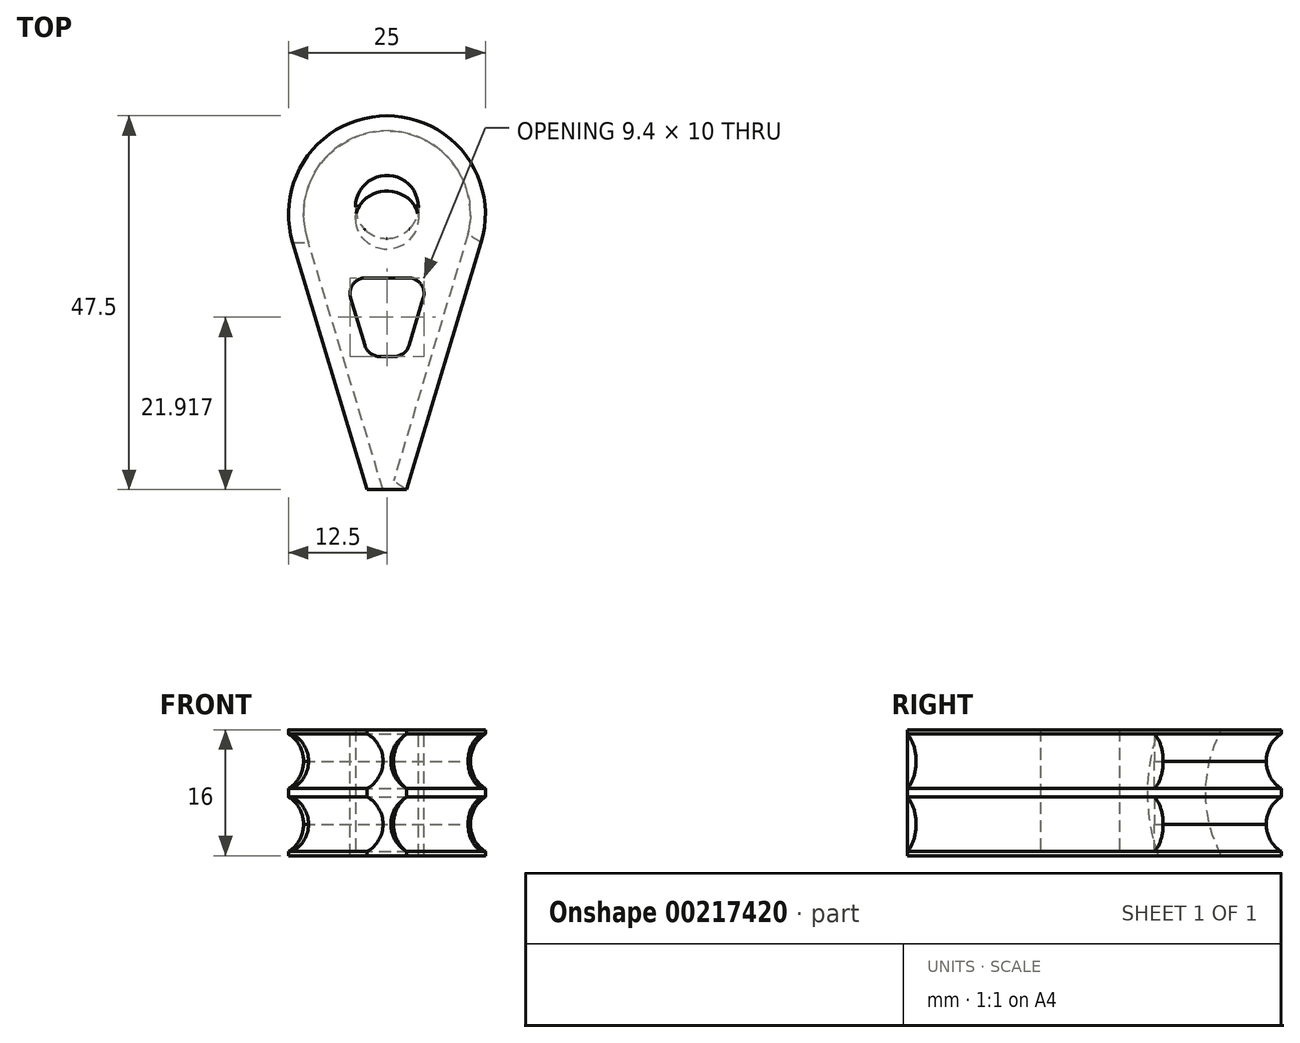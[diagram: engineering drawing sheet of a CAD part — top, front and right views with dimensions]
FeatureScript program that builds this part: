
annotation { "Feature Type Name" : "Feature", "Feature Type Description" : "" }
export const myFeature = defineFeature(function(context is Context, id is Id, definition is map)
    precondition{}
    {
        {
            var Q0;
            Q0=qCreatedBy(makeId("Top.planeOp"),FACE);
            var sketch = newSketch(context, id + "F0", { "sketchPlane" : qUnion([Q0])});
            skArc(sketch, "E0", {"start": v(11.97, -3.6) * mm, "mid": v(0, 12.5) * mm, "end": v(-11.97, -3.6) * mm});
            skLineSegment(sketch, "E1", {"start": v(-11.97, -3.6) * mm, "end": v(-2.5, -35) * mm});
            skLineSegment(sketch, "E2", {"start": v(-2.5, -35) * mm, "end": v(2.5, -35) * mm});
            skLineSegment(sketch, "E3", {"start": v(2.5, -35) * mm, "end": v(11.97, -3.6) * mm});
            skSolve(sketch);
        }
        {
            var Q0;
            Q0=makeQuery(id+"F0.imprint","IMPRINT",FACE,{"disambiguationData":[TD([[makeQuery(id+"F0.imprint","IMPRINT",EDGE,{"derivedFrom":sQuery(id+"F0.wireOp",EDGE,"E0")}),1.0]])]});
            extrude(context, id + "F1", {"entities" : qUnion([Q0]), "depth" : 4 * mm});
        }
        {
            var Q0;
            Q0=makeQuery(id+"F1.opExtrude","CAP_FACE",FACE,{"disambiguationData":[OSD([sQuery(id+"F0.wireOp",EDGE,"C9fcvXtV-jNcn-DBfI-eW0K-3YuiEhr3QxEZ"),sQuery(id+"F0.wireOp",EDGE,"E0"),sQuery(id+"F0.wireOp",EDGE,"E1"),sQuery(id+"F0.wireOp",EDGE,"E2"),sQuery(id+"F0.wireOp",EDGE,"E3")])],"isStart":false});
            var sketch = newSketch(context, id + "F2", { "sketchPlane" : qUnion([Q0])});
            skLineSegment(sketch, "E4", {"start": v(2.5, -35) * mm, "end": v(0.34, -42.16) * mm});
            skSolve(sketch);
        }
        {
            var Q0;
            Q0=makeQuery(id+"F1.opExtrude","SWEPT_FACE",FACE,{"disambiguationData":[OSD([sQuery(id+"F0.wireOp",EDGE,"E2")])]});
            var sketch = newSketch(context, id + "F3", { "sketchPlane" : qUnion([Q0])});
            skCircle(sketch, "E5", {"center": v(-4.5, 4) * mm, "radius": 4 * mm});
            skSolve(sketch);
        }
        {
            var Q0;
            {var subQ0=sQuery(id+"F3.wireOp",EDGE,"E5");var subQ1=sQuery(id+"F0.wireOp",EDGE,"E2");var subQ4=makeQuery(id+"F1.opExtrude","CAP_EDGE",EDGE,{"disambiguationData":[OSD([subQ1])],"isStart":false});var subQ5=makeQuery(id+"F3.imprint","INTERSECT",VERTEX,{"derivedFrom":[subQ4,subQ0]});Q0=makeQuery(id+"F3.imprint","IMPRINT",FACE,{"disambiguationData":[TD([[makeQuery(id+"F3.imprint","IMPRINT",EDGE,{"disambiguationData":[TD([[subQ5,1.0]])],"derivedFrom":subQ0}),1.0]])]});}
            var Q1;
            Q1=sQuery(id+"F3.wireOp",EDGE,"E5");
            var Q2;
            Q2=makeQuery(id+"F1.opExtrude","CAP_EDGE",EDGE,{"disambiguationData":[OSD([sQuery(id+"F0.wireOp",EDGE,"E1")])],"isStart":false});
            var Q3;
            Q3=makeQuery(id+"F1.opExtrude","CAP_EDGE",EDGE,{"disambiguationData":[OSD([sQuery(id+"F0.wireOp",EDGE,"E0")])],"isStart":false});
            var Q4;
            Q4=makeQuery(id+"F1.opExtrude","CAP_EDGE",EDGE,{"disambiguationData":[OSD([sQuery(id+"F0.wireOp",EDGE,"E3")])],"isStart":false});
            var Q5;
            Q5=sQuery(id+"F2.wireOp",EDGE,"E4");
            sweep(context, id + "F4", {"operationType" : NewBodyOperationType.REMOVE, "profiles" : qUnion([Q0]), "surfaceProfiles" : qUnion([Q1]), "path" : qUnion([Q2, Q3, Q4, Q5])});
        }
        {
            var Q0;
            Q0=makeQuery(id+"F1.opExtrude","SWEPT_BODY",BODY,{"disambiguationData":[OSD([sQuery(id+"F0.wireOp",EDGE,"C9fcvXtV-jNcn-DBfI-eW0K-3YuiEhr3QxEZ"),sQuery(id+"F0.wireOp",EDGE,"E0"),sQuery(id+"F0.wireOp",EDGE,"E1"),sQuery(id+"F0.wireOp",EDGE,"E2"),sQuery(id+"F0.wireOp",EDGE,"E3")])]});
            var Q1;
            Q1=makeQuery(id+"F1.opExtrude","CAP_FACE",FACE,{"disambiguationData":[OSD([sQuery(id+"F0.wireOp",EDGE,"C9fcvXtV-jNcn-DBfI-eW0K-3YuiEhr3QxEZ"),sQuery(id+"F0.wireOp",EDGE,"E0"),sQuery(id+"F0.wireOp",EDGE,"E1"),sQuery(id+"F0.wireOp",EDGE,"E2"),sQuery(id+"F0.wireOp",EDGE,"E3")])],"isStart":false});
            mirror(context, id + "F5", {"operationType" : NewBodyOperationType.ADD, "entities" : qUnion([Q0]), "mirrorPlane" : qUnion([Q1])});
        }
        {
            var Q0;
            Q0=makeQuery(id+"F1.opExtrude","SWEPT_BODY",BODY,{"disambiguationData":[OSD([sQuery(id+"F0.wireOp",EDGE,"E0"),sQuery(id+"F0.wireOp",EDGE,"E1"),sQuery(id+"F0.wireOp",EDGE,"E2"),sQuery(id+"F0.wireOp",EDGE,"E3")])]});
            var Q1;
            Q1=makeQuery(id+"F1.opExtrude","CAP_FACE",FACE,{"disambiguationData":[OSD([sQuery(id+"F0.wireOp",EDGE,"E0"),sQuery(id+"F0.wireOp",EDGE,"E1"),sQuery(id+"F0.wireOp",EDGE,"E2"),sQuery(id+"F0.wireOp",EDGE,"E3")])],"isStart":true});
            mirror(context, id + "F6", {"operationType" : NewBodyOperationType.ADD, "entities" : qUnion([Q0]), "mirrorPlane" : qUnion([Q1])});
        }
        {
            var Q0;
            Q0=qCreatedBy(makeId("Right.planeOp"),FACE);
            var sketch = newSketch(context, id + "F7", { "sketchPlane" : qUnion([Q0])});
            skCircle(sketch, "E6", {"center": v(20, 0) * mm, "radius": 20 * mm});
            skSolve(sketch);
        }
        {
            var Q0;
            Q0=makeQuery(id+"F6.opPattern","COPY",FACE,{"derivedFrom":makeQuery(id+"F5.opPattern","COPY",FACE,{"derivedFrom":makeQuery(id+"F1.opExtrude","CAP_FACE",FACE,{"disambiguationData":[OSD([sQuery(id+"F0.wireOp",EDGE,"E0"),sQuery(id+"F0.wireOp",EDGE,"E1"),sQuery(id+"F0.wireOp",EDGE,"E2"),sQuery(id+"F0.wireOp",EDGE,"E3")])],"isStart":true}),"instanceName":"1"}),"instanceName":"1"});
            var sketch = newSketch(context, id + "F8", { "sketchPlane" : qUnion([Q0])});
            skCircle(sketch, "E7", {"center": v(0, -0.92) * mm, "radius": 4 * mm});
            skSolve(sketch);
        }
        {
            var Q0;
            Q0=makeQuery(id+"F8.imprint","IMPRINT",FACE,{"disambiguationData":[TD([[makeQuery(id+"F8.imprint","IMPRINT",EDGE,{"derivedFrom":sQuery(id+"F8.wireOp",EDGE,"E7")}),1.0]])]});
            var Q1;
            Q1=sQuery(id+"F7.wireOp",EDGE,"E6");
            sweep(context, id + "F9", {"operationType" : NewBodyOperationType.REMOVE, "profiles" : qUnion([Q0]), "path" : qUnion([Q1])});
        }
        {
            var Q0;
            Q0=makeQuery(id+"F6.opPattern","COPY",FACE,{"derivedFrom":makeQuery(id+"F5.opPattern","COPY",FACE,{"derivedFrom":makeQuery(id+"F1.opExtrude","CAP_FACE",FACE,{"disambiguationData":[OSD([sQuery(id+"F0.wireOp",EDGE,"E0"),sQuery(id+"F0.wireOp",EDGE,"E1"),sQuery(id+"F0.wireOp",EDGE,"E2"),sQuery(id+"F0.wireOp",EDGE,"E3")])],"isStart":true}),"instanceName":"1"}),"instanceName":"1"});
            var sketch = newSketch(context, id + "F10", { "sketchPlane" : qUnion([Q0])});
            skLineSegment(sketch, "E8.0", {"start": v(2.38, 18.08) * mm, "end": v(7.18, 2.17) * mm});
            skLineSegment(sketch, "E8.1", {"start": v(-7.18, 2.17) * mm, "end": v(-2.38, 18.08) * mm});
            skLineSegment(sketch, "E9", {"start": v(5.4, 8.08) * mm, "end": v(-5.4, 8.08) * mm});
            skLineSegment(sketch, "E10", {"start": v(-2.38, 18.08) * mm, "end": v(2.38, 18.08) * mm});
            skSolve(sketch);
        }
        {
            var Q0;
            Q0=qSketchRegion(id+"F10",true);
            extrude(context, id + "F11", {"entities" : qUnion([Q0]), "operationType" : NewBodyOperationType.REMOVE, "endBound" : BoundingType.UP_TO_NEXT, "oppositeDirection" : true, "depth" : 25 * mm});
        }
        {
            var Q0;
            Q0=makeQuery(id+"F11.boolean.opBoolean","COPY",EDGE,{"derivedFrom":makeQuery(id+"F11.opExtrude","SWEPT_EDGE",EDGE,{"disambiguationData":[OSD([sQuery(id+"F10.wireOp",EDGE,"E8.1"),sQuery(id+"F10.wireOp",EDGE,"E9")])]})});
            var Q1;
            Q1=makeQuery(id+"F11.boolean.opBoolean","COPY",EDGE,{"derivedFrom":makeQuery(id+"F11.opExtrude","SWEPT_EDGE",EDGE,{"disambiguationData":[OSD([sQuery(id+"F10.wireOp",EDGE,"E8.0"),sQuery(id+"F10.wireOp",EDGE,"E9")])]})});
            var Q2;
            Q2=makeQuery(id+"F11.boolean.opBoolean","COPY",EDGE,{"derivedFrom":makeQuery(id+"F11.opExtrude","SWEPT_EDGE",EDGE,{"disambiguationData":[OSD([sQuery(id+"F10.wireOp",EDGE,"E8.1"),sQuery(id+"F10.wireOp",EDGE,"E10")])]})});
            var Q3;
            Q3=makeQuery(id+"F11.boolean.opBoolean","COPY",EDGE,{"derivedFrom":makeQuery(id+"F11.opExtrude","SWEPT_EDGE",EDGE,{"disambiguationData":[OSD([sQuery(id+"F10.wireOp",EDGE,"E8.0"),sQuery(id+"F10.wireOp",EDGE,"E10")])]})});
            fillet(context, id + "F12", {"entities" : qUnion([Q0, Q1, Q2, Q3]), "radius" : 2 * mm, "tangentPropagation" : true, "allowEdgeOverflow" : false});
        }
    });
